# Revit family: PVCSIL
name_source: partatom
category: Duct Accessories
revit_build: Autodesk Revit 2015 (Build: 20140606_1530(x64)
units: mm (PartAtom-declared; Revit-internal decimal feet)

## types (6) — shared parameters
Catalogue Pages = http://www.nuaire.info
Classification.Uniclass.Pr.Description = Ductwork accessories
Classification.Uniclass.Pr.Number = Pr_65_65_23
Fax Number = +44(0)2920-858-222
IFCExportAs = IfcFanType
Manufacturer = Nuaire
Manufacturer Name = Nuaire
Maximum Ambient Temperature = 40 °C
OmniClass Number = 23-33 49 13
OmniClass Title = Ventilation Ducts
Postcode = CF83 1NA
Revit Family Last Revised = 31/10/18
Telephone Number = +44(0)2920-858-200
URL = http://www.nuaire.co.uk
VAT Registration Number = 877308
Warranty Period = 5 Years
Weatherproof or Internal Only = Internal
seal_204 = flat_self_seal_connector_do_not_use : SS-PP-204X60
seal_220 = flat_self_seal_connector_do_not_use : SS-PP-220X90
simple_204 = flat_channel_connector_do_not_use : PVC520WH
simple_220 = flat_channel_connector_do_not_use : PVC920WH

## per-type parameters (varying)
| type | 1or3lengths | 2lengths | 2or3lengths | 3lengths | Description | Duct Connection Height | Duct Connection Width | Height | Length | Unit Description | Weight | Width |
| PVCSIL-500 | Yes | No | No | No | 500mm Long 204x60 Attenuator | 60 mm  [stored 0.19685 ft] | 204 mm  [stored 0.669291 ft] | 60 mm  [stored 0.19685 ft] | 500 mm  [stored 1.64042 ft] | 500mm Long 204x60 Attenuator | 1.80 kg | 204 mm  [stored 0.669291 ft] |
| PVCSIL-1000 | No | Yes | Yes | No | 1000mm Long 204x60 Attenuator | 60 mm  [stored 0.19685 ft] | 204 mm  [stored 0.669291 ft] | 60 mm  [stored 0.19685 ft] | 1000 mm  [stored 3.28084 ft] | 1000mm Long 204x60 Attenuator | 2.80 kg | 204 mm  [stored 0.669291 ft] |
| PVCSIL-1500 | Yes | No | Yes | Yes | 1500mm Long 204x60 Attenuator | 60 mm  [stored 0.19685 ft] | 204 mm  [stored 0.669291 ft] | 60 mm  [stored 0.19685 ft] | 1500 mm  [stored 4.92126 ft] | 1500mm Long 204x60 Attenuator | 3.80 kg | 204 mm  [stored 0.669291 ft] |
| PVCSIL220X90-1500 | Yes | No | Yes | Yes | 1500mm Long 220x90 Attenuator | 90 mm  [stored 0.295276 ft] | 220 mm  [stored 0.721785 ft] | 90 mm  [stored 0.295276 ft] | 1500 mm  [stored 4.92126 ft] | 1500mm Long 220x90 Attenuator | 0.00 kg | 220 mm  [stored 0.721785 ft] |
| PVCSIL220X90-1000 | No | Yes | Yes | No | 1000mm Long 220x90 Attenuator | 90 mm  [stored 0.295276 ft] | 220 mm  [stored 0.721785 ft] | 90 mm  [stored 0.295276 ft] | 1000 mm  [stored 3.28084 ft] | 1000mm Long 220x90 Attenuator | 0.00 kg | 220 mm  [stored 0.721785 ft] |
| PVCSIL220X90-500 | Yes | No | No | No | 1500mm Long 220x90 Attenuator | 90 mm  [stored 0.295276 ft] | 220 mm  [stored 0.721785 ft] | 90 mm  [stored 0.295276 ft] | 500 mm  [stored 1.64042 ft] | 1500mm Long 220x90 Attenuator | 0.00 kg | 220 mm  [stored 0.721785 ft] |

note: column(s) folded — value = type name in every type: Model, Nuaire Model No, Supplier Part No

note: [stored X ft] marks values corroborated as IEEE doubles in the binary element streams (Revit-internal decimal feet)

## geometry (parser evidence)
native form markers: Blend x8, Sweep x10
no freeform markers — native parametric forms only
